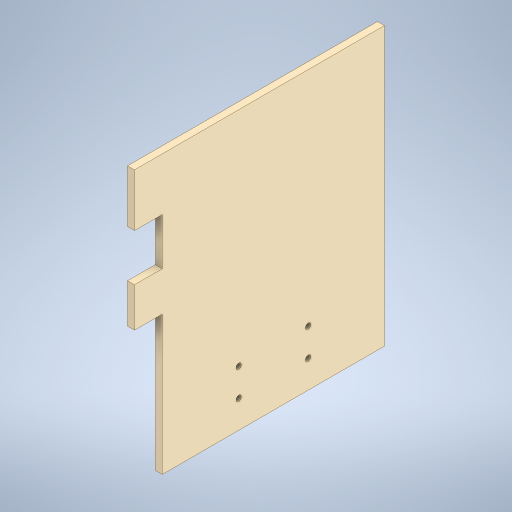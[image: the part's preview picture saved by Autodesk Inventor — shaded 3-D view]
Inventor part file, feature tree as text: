
AUTODESK INVENTOR PART (.ipt)
format: ipt  version: 2024 (Build 280153000, 153)  size: 257,536 bytes
history: native  units: mm
features: extrude x4, sketch x2, projected_geometry x1
ambient origin geometry x8: Origin, YZ Plane, XZ Plane, XY Plane, X Axis, Y Axis, Z Axis, Center Point
bodies: Solid1 (feature_tree)
feature tree (7):
  extrude  "Extrusion1"  Depth=508.0mm
  extrude  "Extrusion2"  Depth=50.8mm
  extrude  "Extrusion3"  Depth=10.0mm
  extrude  "Extrusion4"  Depth=254.0mm
  projected_geometry  "Projected Loop1"
  sketch  "Sketch3"  dims[d0=406.4mm d1=508.0mm]
  sketch  "Sketch4"  dims[d2=12.7mm d3=0.0mm d4=20.0mm d6=127.0mm d7=20.0mm d9=50.8mm d12=10.0mm d14=63.5mm d15=50.8mm d16=12.7mm d17=0.0mm d18=50.8mm d19=0.0mm d20=0.0mm d21=96.2mm d22=50.8mm d23=85.8mm d24=50.8mm d25=0.0mm d26=254.0mm]
